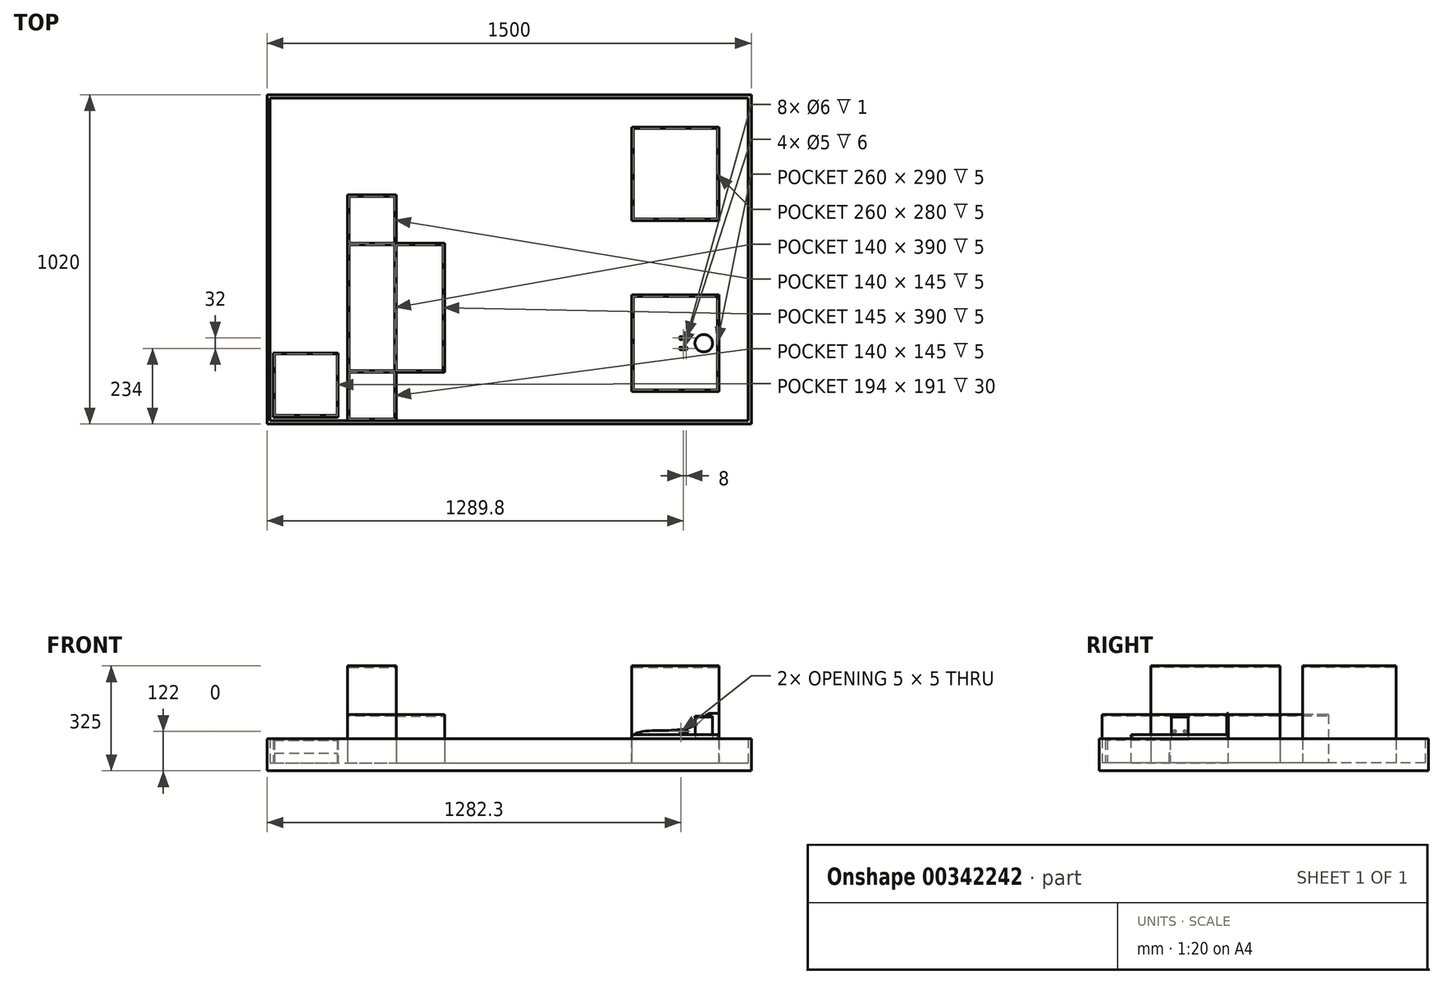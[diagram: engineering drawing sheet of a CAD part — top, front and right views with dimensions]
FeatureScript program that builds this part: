
annotation { "Feature Type Name" : "Feature", "Feature Type Description" : "" }
export const myFeature = defineFeature(function(context is Context, id is Id, definition is map)
    precondition{}
    {
        {
            var Q0;
            Q0=qCreatedBy(makeId("Top.planeOp"),FACE);
            var sketch = newSketch(context, id + "F0", { "sketchPlane" : qUnion([Q0])});
            skCircle(sketch, "E0", {"center": v(0, 0) * mm, "radius": 27.2 * mm});
            skSolve(sketch);
        }
        {
            var Q0;
            Q0=qSketchRegion(id+"F0",true);
            extrude(context, id + "F1", {"entities" : qUnion([Q0]), "depth" : 2.83 * mm});
        }
        {
            var Q0;
            Q0=makeQuery(id+"F1.opExtrude","CAP_FACE",FACE,{"disambiguationData":[OSD([sQuery(id+"F0.wireOp",EDGE,"E0")])],"isStart":false});
            var sketch = newSketch(context, id + "F2", { "sketchPlane" : qUnion([Q0])});
            skCircle(sketch, "E1", {"center": v(0, 0) * mm, "radius": 26.4 * mm});
            skSolve(sketch);
        }
        {
            var Q0;
            Q0=qSketchRegion(id+"F2",true);
            extrude(context, id + "F3", {"entities" : qUnion([Q0]), "operationType" : NewBodyOperationType.ADD, "depth" : 67.36 * mm});
        }
        {
            var Q0;
            Q0=makeQuery(id+"F3.opExtrude","CAP_FACE",FACE,{"disambiguationData":[OSD([sQuery(id+"F2.wireOp",EDGE,"E1")])],"isStart":false});
            var sketch = newSketch(context, id + "F4", { "sketchPlane" : qUnion([Q0])});
            skCircle(sketch, "E2", {"center": v(0, 0) * mm, "radius": 27.2 * mm});
            skSolve(sketch);
        }
        {
            var Q0;
            Q0=qSketchRegion(id+"F4",true);
            extrude(context, id + "F5", {"entities" : qUnion([Q0]), "operationType" : NewBodyOperationType.ADD, "depth" : 2.83 * mm});
        }
        {
            var Q0;
            Q0=makeQuery(id+"F5.opExtrude","CAP_FACE",FACE,{"disambiguationData":[OSD([sQuery(id+"F4.wireOp",EDGE,"E2")])],"isStart":false});
            var sketch = newSketch(context, id + "F6", { "sketchPlane" : qUnion([Q0])});
            skSolve(sketch);
        }
        {
            var Q0;
            Q0=qCreatedBy(makeId("Top.planeOp"),FACE);
            cPlane(context, id + "F7", {"entities" : qUnion([Q0]), "cplaneType" : CPlaneType.OFFSET, "offset" : 25 * mm, "width" : 150 * mm, "height" : 150 * mm});
        }
        {
            var Q0;
            Q0=makeQuery(id+"F6.imprint","IMPRINT",FACE,{"disambiguationData":[TD([[makeQuery(id+"F6.imprint","IMPRINT",EDGE,{"derivedFrom":makeQuery(id+"F5.opExtrude","CAP_EDGE",EDGE,{"disambiguationData":[OSD([sQuery(id+"F4.wireOp",EDGE,"E2")])],"isStart":false})}),1.0]])]});
            var sketch = newSketch(context, id + "F8", { "sketchPlane" : qUnion([Q0])});
            skSolve(sketch);
        }
        {
            var Q0;
            Q0=qCreatedBy(makeId("Top.planeOp"),FACE);
            var sketch = newSketch(context, id + "F9", { "sketchPlane" : qUnion([Q0])});
            skLineSegment(sketch, "E3.bottom", {"start": v(-222.8, -150) * mm, "end": v(47.2, -150) * mm});
            skLineSegment(sketch, "E3.top", {"start": v(-222.8, 150) * mm, "end": v(47.2, 150) * mm});
            skLineSegment(sketch, "E3.left", {"start": v(-222.8, -150) * mm, "end": v(-222.8, 150) * mm});
            skLineSegment(sketch, "E3.right", {"start": v(47.2, -150) * mm, "end": v(47.2, 150) * mm});
            skSolve(sketch);
        }
        {
            var Q0;
            Q0=qSketchRegion(id+"F9",true);
            extrude(context, id + "F10", {"entities" : qUnion([Q0]), "oppositeDirection" : true, "depth" : 72 * mm});
        }
        {
            var Q0;
            Q0=makeQuery(id+"F10.opExtrude","CAP_FACE",FACE,{"disambiguationData":[OSD([sQuery(id+"F9.wireOp",EDGE,"E3.bottom"),sQuery(id+"F9.wireOp",EDGE,"E3.top"),sQuery(id+"F9.wireOp",EDGE,"E3.left"),sQuery(id+"F9.wireOp",EDGE,"E3.right")])],"isStart":true});
            var sketch = newSketch(context, id + "F11", { "sketchPlane" : qUnion([Q0])});
            skLineSegment(sketch, "E4.bottom", {"start": v(-222.8, -150) * mm, "end": v(47.2, -150) * mm});
            skLineSegment(sketch, "E4.top", {"start": v(-222.8, -145) * mm, "end": v(42.2, -145) * mm});
            skLineSegment(sketch, "E4.left", {"start": v(-222.8, -150) * mm, "end": v(-222.8, -145) * mm});
            skLineSegment(sketch, "E5.bottom", {"start": v(47.2, 150) * mm, "end": v(42.2, 150) * mm});
            skLineSegment(sketch, "E5.left", {"start": v(47.2, 150) * mm, "end": v(47.2, -150) * mm});
            skLineSegment(sketch, "E5.right", {"start": v(42.2, 150) * mm, "end": v(42.2, -145) * mm});
            skSolve(sketch);
        }
        {
            var Q0;
            Q0=qSketchRegion(id+"F11",true);
            extrude(context, id + "F12", {"entities" : qUnion([Q0]), "operationType" : NewBodyOperationType.ADD, "depth" : 15 * mm});
        }
        {
            var Q0;
            Q0=makeQuery(id+"F12.boolean.opBoolean","MERGE",FACE,{"derivedFrom":[makeQuery(id+"F10.opExtrude","SWEPT_FACE",FACE,{"disambiguationData":[OSD([sQuery(id+"F9.wireOp",EDGE,"E3.top")])]}),makeQuery(id+"F12.opExtrude","SWEPT_FACE",FACE,{"disambiguationData":[OSD([sQuery(id+"F11.wireOp",EDGE,"E5.bottom")])]})]});
            var sketch = newSketch(context, id + "F13", { "sketchPlane" : qUnion([Q0])});
            skLineSegment(sketch, "E6", {"start": v(-47.2, 81.36) * mm, "end": v(-21.31, 81.36) * mm});
            skFitSpline(sketch, "E7", {"points": [v(-21.31, 81.36) * mm, v(15.24, 52.01) * mm, v(114.14, 28.17) * mm, v(222.8, 0) * mm], "startDerivative": vector(181.02, 0.3) * mm, "endDerivative": vector(-1.73, -239.85) * mm});
            skLineSegment(sketch, "E8", {"start": v(-47.2, 81.36) * mm, "end": v(-47.2, -72) * mm});
            skLineSegment(sketch, "E9", {"start": v(-47.2, -72) * mm, "end": v(222.8, -72) * mm});
            skLineSegment(sketch, "E10", {"start": v(222.8, -72) * mm, "end": v(222.8, 0) * mm});
            skSolve(sketch);
        }
        {
            var Q0;
            Q0=qSketchRegion(id+"F13",true);
            extrude(context, id + "F14", {"entities" : qUnion([Q0]), "operationType" : NewBodyOperationType.ADD, "oppositeDirection" : true, "depth" : 5 * mm});
        }
        {
            var Q0;
            Q0=makeQuery(id+"F10.opExtrude","CAP_FACE",FACE,{"disambiguationData":[OSD([sQuery(id+"F9.wireOp",EDGE,"E3.bottom"),sQuery(id+"F9.wireOp",EDGE,"E3.top"),sQuery(id+"F9.wireOp",EDGE,"E3.left"),sQuery(id+"F9.wireOp",EDGE,"E3.right")])],"isStart":true});
            var sketch = newSketch(context, id + "F15", { "sketchPlane" : qUnion([Q0])});
            skLineSegment(sketch, "E11.bottom", {"start": v(-222.8, 145) * mm, "end": v(-217.8, 145) * mm});
            skLineSegment(sketch, "E11.top", {"start": v(-222.8, -145) * mm, "end": v(-217.8, -145) * mm});
            skLineSegment(sketch, "E11.left", {"start": v(-222.8, 145) * mm, "end": v(-222.8, -145) * mm});
            skLineSegment(sketch, "E11.right", {"start": v(-217.8, 145) * mm, "end": v(-217.8, -145) * mm});
            skSolve(sketch);
        }
        {
            var Q0;
            Q0=qSketchRegion(id+"F15",true);
            extrude(context, id + "F16", {"entities" : qUnion([Q0]), "operationType" : NewBodyOperationType.ADD, "depth" : 5 * mm});
        }
        {
            var Q0;
            Q0=makeQuery(id+"F10.opExtrude","CAP_FACE",FACE,{"disambiguationData":[OSD([sQuery(id+"F9.wireOp",EDGE,"E3.bottom"),sQuery(id+"F9.wireOp",EDGE,"E3.top"),sQuery(id+"F9.wireOp",EDGE,"E3.left"),sQuery(id+"F9.wireOp",EDGE,"E3.right")])],"isStart":false});
            var sketch = newSketch(context, id + "F17", { "sketchPlane" : qUnion([Q0])});
            skLineSegment(sketch, "E12.bottom", {"start": v(147.2, 250) * mm, "end": v(-1352.8, 250) * mm});
            skLineSegment(sketch, "E12.top", {"start": v(147.2, -770) * mm, "end": v(-1352.8, -770) * mm});
            skLineSegment(sketch, "E12.left", {"start": v(147.2, 250) * mm, "end": v(147.2, -770) * mm});
            skLineSegment(sketch, "E12.right", {"start": v(-1352.8, 250) * mm, "end": v(-1352.8, -770) * mm});
            skSolve(sketch);
        }
        {
            var Q0;
            Q0=qSketchRegion(id+"F17",true);
            extrude(context, id + "F18", {"entities" : qUnion([Q0]), "operationType" : NewBodyOperationType.ADD, "depth" : 25 * mm});
        }
        {
            var Q0;
            Q0=makeQuery(id+"F18.opExtrude","CAP_FACE",FACE,{"disambiguationData":[OSD([sQuery(id+"F17.wireOp",EDGE,"E12.bottom"),sQuery(id+"F17.wireOp",EDGE,"E12.top"),sQuery(id+"F17.wireOp",EDGE,"E12.left"),sQuery(id+"F17.wireOp",EDGE,"E12.right")])],"isStart":true});
            var sketch = newSketch(context, id + "F19", { "sketchPlane" : qUnion([Q0])});
            skLineSegment(sketch, "E13.bottom", {"start": v(-222.8, 670) * mm, "end": v(47.2, 670) * mm});
            skLineSegment(sketch, "E13.top", {"start": v(-222.8, 380) * mm, "end": v(47.2, 380) * mm});
            skLineSegment(sketch, "E13.left", {"start": v(-222.8, 670) * mm, "end": v(-222.8, 380) * mm});
            skLineSegment(sketch, "E13.right", {"start": v(47.2, 670) * mm, "end": v(47.2, 380) * mm});
            skSolve(sketch);
        }
        {
            var Q0;
            Q0=qSketchRegion(id+"F19",true);
            extrude(context, id + "F20", {"entities" : qUnion([Q0]), "operationType" : NewBodyOperationType.ADD, "depth" : 300 * mm});
        }
        {
            var Q0;
            Q0=makeQuery(id+"F20.opExtrude","CAP_FACE",FACE,{"disambiguationData":[OSD([sQuery(id+"F19.wireOp",EDGE,"E13.bottom"),sQuery(id+"F19.wireOp",EDGE,"E13.top"),sQuery(id+"F19.wireOp",EDGE,"E13.left"),sQuery(id+"F19.wireOp",EDGE,"E13.right")])],"isStart":false});
            var sketch = newSketch(context, id + "F21", { "sketchPlane" : qUnion([Q0])});
            skLineSegment(sketch, "E14.bottom", {"start": v(-217.8, 665) * mm, "end": v(42.2, 665) * mm});
            skLineSegment(sketch, "E14.top", {"start": v(-217.8, 385) * mm, "end": v(42.2, 385) * mm});
            skLineSegment(sketch, "E14.left", {"start": v(-217.8, 665) * mm, "end": v(-217.8, 385) * mm});
            skLineSegment(sketch, "E14.right", {"start": v(42.2, 665) * mm, "end": v(42.2, 385) * mm});
            skSolve(sketch);
        }
        {
            var Q0;
            Q0=qSketchRegion(id+"F21",true);
            extrude(context, id + "F22", {"entities" : qUnion([Q0]), "operationType" : NewBodyOperationType.REMOVE, "oppositeDirection" : true, "depth" : 5 * mm});
        }
        {
            var Q0;
            Q0=makeQuery(id+"F18.opExtrude","CAP_FACE",FACE,{"disambiguationData":[OSD([sQuery(id+"F17.wireOp",EDGE,"E12.bottom"),sQuery(id+"F17.wireOp",EDGE,"E12.top"),sQuery(id+"F17.wireOp",EDGE,"E12.left"),sQuery(id+"F17.wireOp",EDGE,"E12.right")])],"isStart":true});
            var sketch = newSketch(context, id + "F23", { "sketchPlane" : qUnion([Q0])});
            skLineSegment(sketch, "E15.bottom", {"start": v(-1352.8, 770) * mm, "end": v(147.2, 770) * mm});
            skLineSegment(sketch, "E15.top", {"start": v(-1352.8, -250) * mm, "end": v(147.2, -250) * mm});
            skLineSegment(sketch, "E15.left", {"start": v(-1352.8, 770) * mm, "end": v(-1352.8, -250) * mm});
            skLineSegment(sketch, "E15.right", {"start": v(147.2, 770) * mm, "end": v(147.2, -250) * mm});
            skLineSegment(sketch, "E16.bottom", {"start": v(-1342.8, 760) * mm, "end": v(137.2, 760) * mm});
            skLineSegment(sketch, "E16.top", {"start": v(-1342.8, -240) * mm, "end": v(137.2, -240) * mm});
            skLineSegment(sketch, "E16.left", {"start": v(-1342.8, 760) * mm, "end": v(-1342.8, -240) * mm});
            skLineSegment(sketch, "E16.right", {"start": v(137.2, 760) * mm, "end": v(137.2, -240) * mm});
            skSolve(sketch);
        }
        {
            var Q0;
            Q0=qSketchRegion(id+"F23",true);
            extrude(context, id + "F24", {"entities" : qUnion([Q0]), "operationType" : NewBodyOperationType.ADD, "depth" : 75 * mm});
        }
        {
            var Q0;
            Q0=makeQuery(id+"F18.opExtrude","CAP_FACE",FACE,{"disambiguationData":[OSD([sQuery(id+"F17.wireOp",EDGE,"E12.bottom"),sQuery(id+"F17.wireOp",EDGE,"E12.top"),sQuery(id+"F17.wireOp",EDGE,"E12.left"),sQuery(id+"F17.wireOp",EDGE,"E12.right")])],"isStart":true});
            var sketch = newSketch(context, id + "F25", { "sketchPlane" : qUnion([Q0])});
            skLineSegment(sketch, "E17.bottom", {"start": v(-1102.8, 460) * mm, "end": v(-952.8, 460) * mm});
            skLineSegment(sketch, "E17.top", {"start": v(-1102.8, -240) * mm, "end": v(-952.8, -240) * mm});
            skLineSegment(sketch, "E17.left", {"start": v(-1102.8, 460) * mm, "end": v(-1102.8, -240) * mm});
            skLineSegment(sketch, "E17.right", {"start": v(-952.8, 460) * mm, "end": v(-952.8, 310) * mm});
            skLineSegment(sketch, "E18.bottom", {"start": v(-952.8, 310) * mm, "end": v(-802.8, 310) * mm});
            skLineSegment(sketch, "E18.top", {"start": v(-952.8, -90) * mm, "end": v(-802.8, -90) * mm});
            skLineSegment(sketch, "E18.right", {"start": v(-802.8, 310) * mm, "end": v(-802.8, -90) * mm});
            skLineSegment(sketch, "E19.trimOffspring", {"start": v(-952.8, -90) * mm, "end": v(-952.8, -240) * mm});
            skSolve(sketch);
        }
        {
            var Q0;
            Q0=qSketchRegion(id+"F25",true);
            extrude(context, id + "F26", {"entities" : qUnion([Q0]), "operationType" : NewBodyOperationType.ADD, "depth" : 150 * mm});
        }
        {
            var Q0;
            Q0=makeQuery(id+"F26.opExtrude","CAP_FACE",FACE,{"disambiguationData":[OSD([sQuery(id+"F25.wireOp",EDGE,"E17.bottom"),sQuery(id+"F25.wireOp",EDGE,"E17.top"),sQuery(id+"F25.wireOp",EDGE,"E17.left"),sQuery(id+"F25.wireOp",EDGE,"E17.right"),sQuery(id+"F25.wireOp",EDGE,"E18.bottom"),sQuery(id+"F25.wireOp",EDGE,"E18.top"),sQuery(id+"F25.wireOp",EDGE,"E18.right"),sQuery(id+"F25.wireOp",EDGE,"E19.trimOffspring")])],"isStart":false});
            var sketch = newSketch(context, id + "F27", { "sketchPlane" : qUnion([Q0])});
            skLineSegment(sketch, "E20.bottom", {"start": v(-952.8, 310) * mm, "end": v(-1102.8, 310) * mm});
            skLineSegment(sketch, "E20.top", {"start": v(-952.8, -90) * mm, "end": v(-1102.8, -90) * mm});
            skLineSegment(sketch, "E20.left", {"start": v(-952.8, 310) * mm, "end": v(-952.8, -90) * mm});
            skLineSegment(sketch, "E20.right", {"start": v(-1102.8, 310) * mm, "end": v(-1102.8, -90) * mm});
            skSolve(sketch);
        }
        {
            var Q0;
            Q0=qSketchRegion(id+"F27",true);
            extrude(context, id + "F28", {"entities" : qUnion([Q0]), "operationType" : NewBodyOperationType.ADD, "depth" : 150 * mm});
        }
        {
            var Q0;
            Q0=makeQuery(id+"F28.opExtrude","CAP_FACE",FACE,{"disambiguationData":[OSD([sQuery(id+"F27.wireOp",EDGE,"E20.bottom"),sQuery(id+"F27.wireOp",EDGE,"E20.top"),sQuery(id+"F27.wireOp",EDGE,"E20.left"),sQuery(id+"F27.wireOp",EDGE,"E20.right")])],"isStart":false});
            var sketch = newSketch(context, id + "F29", { "sketchPlane" : qUnion([Q0])});
            skLineSegment(sketch, "E21.bottom", {"start": v(-1097.8, 305) * mm, "end": v(-957.8, 305) * mm});
            skLineSegment(sketch, "E21.top", {"start": v(-1097.8, -85) * mm, "end": v(-957.8, -85) * mm});
            skLineSegment(sketch, "E21.left", {"start": v(-1097.8, 305) * mm, "end": v(-1097.8, -85) * mm});
            skLineSegment(sketch, "E21.right", {"start": v(-957.8, 305) * mm, "end": v(-957.8, -85) * mm});
            skSolve(sketch);
        }
        {
            var Q0;
            Q0=qSketchRegion(id+"F29",true);
            extrude(context, id + "F30", {"entities" : qUnion([Q0]), "operationType" : NewBodyOperationType.REMOVE, "oppositeDirection" : true, "depth" : 5 * mm});
        }
        {
            var Q0;
            {var subQ0=sQuery(id+"F25.wireOp",EDGE,"E17.left");var subQ1=sQuery(id+"F25.wireOp",EDGE,"E18.bottom");var subQ2=sQuery(id+"F25.wireOp",EDGE,"E17.right");var subQ3=sQuery(id+"F25.wireOp",EDGE,"E17.bottom");var subQ4=makeQuery(id+"F26.opExtrude","CAP_FACE",FACE,{"disambiguationData":[OSD([subQ3,sQuery(id+"F25.wireOp",EDGE,"E17.top"),subQ0,subQ2,subQ1,sQuery(id+"F25.wireOp",EDGE,"E18.top"),sQuery(id+"F25.wireOp",EDGE,"E18.right"),sQuery(id+"F25.wireOp",EDGE,"E19.trimOffspring")])],"isStart":false});Q0=makeQuery(id+"F28.boolean.opBoolean","SPLIT",FACE,{"disambiguationData":[TD([makeQuery(id+"F26.opExtrude","SWEPT_FACE",FACE,{"disambiguationData":[OSD([subQ3])]})])],"derivedFrom":subQ4});}
            var sketch = newSketch(context, id + "F31", { "sketchPlane" : qUnion([Q0])});
            skLineSegment(sketch, "E22.bottom", {"start": v(-1097.8, 455) * mm, "end": v(-957.8, 455) * mm});
            skLineSegment(sketch, "E22.top", {"start": v(-1097.8, 310) * mm, "end": v(-957.8, 310) * mm});
            skLineSegment(sketch, "E22.left", {"start": v(-1097.8, 455) * mm, "end": v(-1097.8, 310) * mm});
            skLineSegment(sketch, "E22.right", {"start": v(-957.8, 455) * mm, "end": v(-957.8, 310) * mm});
            skLineSegment(sketch, "E23.bottom", {"start": v(-952.8, 305) * mm, "end": v(-807.8, 305) * mm});
            skLineSegment(sketch, "E23.top", {"start": v(-952.8, -85) * mm, "end": v(-807.8, -85) * mm});
            skLineSegment(sketch, "E23.left", {"start": v(-952.8, 305) * mm, "end": v(-952.8, -85) * mm});
            skLineSegment(sketch, "E23.right", {"start": v(-807.8, 305) * mm, "end": v(-807.8, -85) * mm});
            skLineSegment(sketch, "E24.bottom", {"start": v(-1097.8, -90) * mm, "end": v(-957.8, -90) * mm});
            skLineSegment(sketch, "E24.top", {"start": v(-1097.8, -235) * mm, "end": v(-957.8, -235) * mm});
            skLineSegment(sketch, "E24.left", {"start": v(-1097.8, -90) * mm, "end": v(-1097.8, -235) * mm});
            skLineSegment(sketch, "E24.right", {"start": v(-957.8, -90) * mm, "end": v(-957.8, -235) * mm});
            skSolve(sketch);
        }
        {
            var Q0;
            Q0=qSketchRegion(id+"F31",true);
            extrude(context, id + "F32", {"entities" : qUnion([Q0]), "operationType" : NewBodyOperationType.REMOVE, "oppositeDirection" : true, "depth" : 5 * mm});
        }
        {
            var Q0;
            Q0=qCreatedBy(id+"F7.planeOp",FACE);
            var sketch = newSketch(context, id + "F33", { "sketchPlane" : qUnion([Q0])});
            skLineSegment(sketch, "E25", {"start": v(0, 0) * mm, "end": v(-90, 0) * mm, "construction": true});
            skLineSegment(sketch, "E26.bottom", {"start": v(-74.5, -12) * mm, "end": v(-55, -12) * mm});
            skLineSegment(sketch, "E26.top", {"start": v(-74.5, -20) * mm, "end": v(-55, -20) * mm});
            skLineSegment(sketch, "E26.left", {"start": v(-74.5, -12) * mm, "end": v(-74.5, -13) * mm});
            skPoint(sketch, "E27.visualSharp", {"position": v(-51, -12) * mm});
            skPoint(sketch, "E28.visualSharp", {"position": v(-51, -20) * mm});
            skCircle(sketch, "E29", {"center": v(-55, -16) * mm, "radius": 3 * mm});
            skLineSegment(sketch, "E30", {"start": v(-59, -3.98) * mm, "end": v(-59, -18.08) * mm, "construction": true});
            skCircle(sketch, "E31.MirrorC", {"center": v(-63, -16) * mm, "radius": 3 * mm});
            skLineSegment(sketch, "E32.bottom", {"start": v(-74.5, -13) * mm, "end": v(-65.65, -13) * mm});
            skLineSegment(sketch, "E32.top", {"start": v(-74.5, -19) * mm, "end": v(-65.65, -19) * mm});
            skArc(sketch, "E33", {"start": v(-65.65, -13) * mm, "mid": v(-67, -16) * mm, "end": v(-65.65, -19) * mm});
            skLineSegment(sketch, "E34.trimOffspring", {"start": v(-74.5, -19) * mm, "end": v(-74.5, -20) * mm});
            skArc(sketch, "E35.trimOffspring", {"start": v(-55, -20) * mm, "mid": v(-51, -16) * mm, "end": v(-55, -12) * mm});
            skLineSegment(sketch, "E36.MirrorCS", {"start": v(-74.5, 12) * mm, "end": v(-74.5, 13) * mm});
            skLineSegment(sketch, "E37.MirrorCS", {"start": v(-74.5, 19) * mm, "end": v(-74.5, 20) * mm});
            skPoint(sketch, "E38.MirrorP", {"position": v(-51, 12) * mm});
            skLineSegment(sketch, "E39.MirrorCS", {"start": v(-74.5, 12) * mm, "end": v(-55, 12) * mm});
            skPoint(sketch, "E40.MirrorP", {"position": v(-51, 20) * mm});
            skArc(sketch, "E41.MirrorCS", {"start": v(-65.65, 13) * mm, "mid": v(-67, 16) * mm, "end": v(-65.65, 19) * mm});
            skArc(sketch, "E42.MirrorCS", {"start": v(-55, 20) * mm, "mid": v(-51, 16) * mm, "end": v(-55, 12) * mm});
            skLineSegment(sketch, "E43.MirrorCS", {"start": v(-74.5, 20) * mm, "end": v(-55, 20) * mm});
            skCircle(sketch, "E44.MirrorC", {"center": v(-55, 16) * mm, "radius": 3 * mm});
            skCircle(sketch, "E45.MirrorC", {"center": v(-63, 16) * mm, "radius": 3 * mm});
            skLineSegment(sketch, "E46.MirrorCS", {"start": v(-74.5, 19) * mm, "end": v(-65.65, 19) * mm});
            skLineSegment(sketch, "E47.MirrorCS", {"start": v(-74.5, 13) * mm, "end": v(-65.65, 13) * mm});
            skSolve(sketch);
        }
        {
            var Q0;
            Q0=qSketchRegion(id+"F33",true);
            var Q1;
            Q1=qSketchRegion(id+"F36",true);
            extrude(context, id + "F34", {"entities" : qUnion([Q0, Q1]), "depth" : 8 * mm, "symmetric" : true});
        }
        {
            var Q0;
            Q0=makeQuery(id+"F34.opExtrude","CAP_EDGE",EDGE,{"disambiguationData":[OSD([sQuery(id+"F33.wireOp",EDGE,"E34.trimOffspring")])],"isStart":false});
            var Q1;
            Q1=makeQuery(id+"F34.opExtrude","CAP_EDGE",EDGE,{"disambiguationData":[OSD([sQuery(id+"F33.wireOp",EDGE,"E26.left")])],"isStart":false});
            var Q2;
            Q2=makeQuery(id+"F34.opExtrude","CAP_EDGE",EDGE,{"disambiguationData":[OSD([sQuery(id+"F33.wireOp",EDGE,"E34.trimOffspring")])],"isStart":true});
            var Q3;
            Q3=makeQuery(id+"F34.opExtrude","CAP_EDGE",EDGE,{"disambiguationData":[OSD([sQuery(id+"F33.wireOp",EDGE,"E26.left")])],"isStart":true});
            var Q4;
            Q4=makeQuery(id+"F34.opExtrude","CAP_EDGE",EDGE,{"disambiguationData":[OSD([sQuery(id+"F33.wireOp",EDGE,"E36.MirrorCS")])],"isStart":false});
            var Q5;
            Q5=makeQuery(id+"F34.opExtrude","CAP_EDGE",EDGE,{"disambiguationData":[OSD([sQuery(id+"F33.wireOp",EDGE,"E37.MirrorCS")])],"isStart":false});
            var Q6;
            Q6=makeQuery(id+"F34.opExtrude","CAP_EDGE",EDGE,{"disambiguationData":[OSD([sQuery(id+"F33.wireOp",EDGE,"E37.MirrorCS")])],"isStart":true});
            var Q7;
            Q7=makeQuery(id+"F34.opExtrude","CAP_EDGE",EDGE,{"disambiguationData":[OSD([sQuery(id+"F33.wireOp",EDGE,"E36.MirrorCS")])],"isStart":true});
            fillet(context, id + "F35", {"entities" : qUnion([Q0, Q1, Q2, Q3, Q4, Q5, Q6, Q7]), "radius" : 4 * mm, "tangentPropagation" : true, "allowEdgeOverflow" : false});
        }
        {
            var Q0;
            Q0=makeQuery(id+"F34.opExtrude","SWEPT_FACE",FACE,{"disambiguationData":[OSD([sQuery(id+"F33.wireOp",EDGE,"E26.top")])]});
            var sketch = newSketch(context, id + "F36", { "sketchPlane" : qUnion([Q0])});
            skCircle(sketch, "E48", {"center": v(-70.5, 25) * mm, "radius": 3 * mm});
            skSolve(sketch);
        }
        {
            var Q0;
            Q0=qSketchRegion(id+"F36",true);
            var Q1;
            Q1=makeQuery(id+"F34.opExtrude","SWEPT_FACE",FACE,{"disambiguationData":[OSD([sQuery(id+"F33.wireOp",EDGE,"E26.bottom")])]});
            extrude(context, id + "F37", {"entities" : qUnion([Q0]), "operationType" : NewBodyOperationType.ADD, "endBound" : BoundingType.UP_TO_SURFACE, "oppositeDirection" : true, "endBoundEntityFace" : qUnion([Q1]), "depth" : 25 * mm});
        }
        {
            var Q0;
            Q0=makeQuery(id+"F34.opExtrude","SWEPT_FACE",FACE,{"disambiguationData":[OSD([sQuery(id+"F33.wireOp",EDGE,"E43.MirrorCS")])]});
            var sketch = newSketch(context, id + "F38", { "sketchPlane" : qUnion([Q0])});
            skCircle(sketch, "E49", {"center": v(70.5, 25) * mm, "radius": 3 * mm});
            skSolve(sketch);
        }
        {
            var Q0;
            Q0=qSketchRegion(id+"F38",true);
            var Q1;
            Q1=makeQuery(id+"F34.opExtrude","SWEPT_FACE",FACE,{"disambiguationData":[OSD([sQuery(id+"F33.wireOp",EDGE,"E39.MirrorCS")])]});
            extrude(context, id + "F39", {"entities" : qUnion([Q0]), "operationType" : NewBodyOperationType.ADD, "endBound" : BoundingType.UP_TO_SURFACE, "oppositeDirection" : true, "endBoundEntityFace" : qUnion([Q1]), "depth" : 25 * mm});
        }
        {
            var Q0;
            Q0=qCreatedBy(id+"F7.planeOp",FACE);
            var sketch = newSketch(context, id + "F40", { "sketchPlane" : qUnion([Q0])});
            skCircle(sketch, "E50", {"center": v(-55, 16) * mm, "radius": 3 * mm});
            skCircle(sketch, "E51", {"center": v(-63, 16) * mm, "radius": 2.5 * mm});
            skCircle(sketch, "E52", {"center": v(-63, 16) * mm, "radius": 3 * mm});
            skCircle(sketch, "E53", {"center": v(-55, 16) * mm, "radius": 2.5 * mm});
            skSolve(sketch);
        }
        {
            var Q0;
            Q0=qSketchRegion(id+"F40",true);
            extrude(context, id + "F41", {"entities" : qUnion([Q0]), "operationType" : NewBodyOperationType.ADD, "depth" : 6 * mm, "symmetric" : true});
        }
        {
            var Q0;
            Q0=qCreatedBy(id+"F7.planeOp",FACE);
            var sketch = newSketch(context, id + "F42", { "sketchPlane" : qUnion([Q0])});
            skCircle(sketch, "E54", {"center": v(-63, -16) * mm, "radius": 2.5 * mm});
            skCircle(sketch, "E55", {"center": v(-63, -16) * mm, "radius": 3 * mm});
            skCircle(sketch, "E56", {"center": v(-55, -16) * mm, "radius": 2.5 * mm});
            skCircle(sketch, "E57", {"center": v(-55, -16) * mm, "radius": 3 * mm});
            skSolve(sketch);
        }
        {
            var Q0;
            Q0=qSketchRegion(id+"F42",true);
            extrude(context, id + "F43", {"entities" : qUnion([Q0]), "operationType" : NewBodyOperationType.ADD, "depth" : 6 * mm, "symmetric" : true});
        }
        {
            var Q0;
            Q0=makeQuery(id+"F34.opExtrude","SWEPT_FACE",FACE,{"disambiguationData":[OSD([sQuery(id+"F33.wireOp",EDGE,"E43.MirrorCS")])]});
            var sketch = newSketch(context, id + "F44", { "sketchPlane" : qUnion([Q0])});
            skArc(sketch, "E58", {"start": v(71.5, 27.3) * mm, "mid": v(70.5, 27.5) * mm, "end": v(69.5, 27.3) * mm});
            skLineSegment(sketch, "E59.bottom", {"start": v(68.2, 26) * mm, "end": v(69.5, 26) * mm});
            skLineSegment(sketch, "E59.top", {"start": v(68.2, 24) * mm, "end": v(69.5, 24) * mm});
            skLineSegment(sketch, "E60.left", {"start": v(71.5, 27.3) * mm, "end": v(71.5, 26) * mm});
            skLineSegment(sketch, "E60.right", {"start": v(69.5, 27.3) * mm, "end": v(69.5, 26) * mm});
            skPoint(sketch, "E61.orphan", {"position": v(69.5, 27.8) * mm});
            skPoint(sketch, "E62.orphan", {"position": v(71.5, 27.8) * mm});
            skArc(sketch, "E63.trimOffspring", {"start": v(68.2, 26) * mm, "mid": v(68, 25) * mm, "end": v(68.2, 24) * mm});
            skPoint(sketch, "E59.left.start.orphan", {"position": v(67.32, 26) * mm});
            skPoint(sketch, "E64.orphan", {"position": v(67.32, 24) * mm});
            skArc(sketch, "E65.trimOffspring", {"start": v(69.5, 22.7) * mm, "mid": v(70.5, 22.5) * mm, "end": v(71.5, 22.7) * mm});
            skLineSegment(sketch, "E66.trimOffspring", {"start": v(69.5, 24) * mm, "end": v(69.5, 22.7) * mm});
            skLineSegment(sketch, "E67.trimOffspring", {"start": v(71.5, 26) * mm, "end": v(72.8, 26) * mm});
            skLineSegment(sketch, "E68.trimOffspring", {"start": v(71.5, 24) * mm, "end": v(71.5, 22.7) * mm});
            skLineSegment(sketch, "E69.trimOffspring", {"start": v(71.5, 24) * mm, "end": v(72.8, 24) * mm});
            skPoint(sketch, "E60.top.end.orphan", {"position": v(69.5, 22.2) * mm});
            skPoint(sketch, "E70.orphan", {"position": v(71.5, 22.2) * mm});
            skPoint(sketch, "E59.right.end.orphan", {"position": v(73.68, 24) * mm});
            skPoint(sketch, "E71.orphan", {"position": v(73.68, 26) * mm});
            skArc(sketch, "E72.trimOffspring", {"start": v(72.8, 24) * mm, "mid": v(73, 25) * mm, "end": v(72.8, 26) * mm});
            skSolve(sketch);
        }
        {
            var Q0;
            Q0=qSketchRegion(id+"F44",true);
            extrude(context, id + "F45", {"entities" : qUnion([Q0]), "operationType" : NewBodyOperationType.REMOVE, "endBound" : BoundingType.THROUGH_ALL, "oppositeDirection" : true, "depth" : 25 * mm});
        }
        {
            var Q0;
            Q0=makeQuery(id+"F18.opExtrude","CAP_FACE",FACE,{"disambiguationData":[OSD([sQuery(id+"F17.wireOp",EDGE,"E12.bottom"),sQuery(id+"F17.wireOp",EDGE,"E12.top"),sQuery(id+"F17.wireOp",EDGE,"E12.left"),sQuery(id+"F17.wireOp",EDGE,"E12.right")])],"isStart":true});
            var sketch = newSketch(context, id + "F46", { "sketchPlane" : qUnion([Q0])});
            skLineSegment(sketch, "E73.bottom", {"start": v(-1332.8, -30) * mm, "end": v(-1132.8, -30) * mm});
            skLineSegment(sketch, "E73.top", {"start": v(-1332.8, -230) * mm, "end": v(-1132.8, -230) * mm});
            skLineSegment(sketch, "E73.left", {"start": v(-1332.8, -30) * mm, "end": v(-1332.8, -230) * mm});
            skLineSegment(sketch, "E73.right", {"start": v(-1132.8, -30) * mm, "end": v(-1132.8, -230) * mm});
            skLineSegment(sketch, "E74.bottom", {"start": v(-1329.8, -33) * mm, "end": v(-1135.8, -33) * mm});
            skLineSegment(sketch, "E74.top", {"start": v(-1329.8, -224) * mm, "end": v(-1135.8, -224) * mm});
            skLineSegment(sketch, "E74.left", {"start": v(-1329.8, -33) * mm, "end": v(-1329.8, -224) * mm});
            skLineSegment(sketch, "E74.right", {"start": v(-1135.8, -33) * mm, "end": v(-1135.8, -224) * mm});
            skSolve(sketch);
        }
        {
            var Q0;
            Q0=qSketchRegion(id+"F46",true);
            extrude(context, id + "F47", {"entities" : qUnion([Q0]), "operationType" : NewBodyOperationType.ADD, "depth" : 30 * mm});
        }
        {
            var Q0;
            Q0=makeQuery(id+"F47.opExtrude","CAP_FACE",FACE,{"disambiguationData":[OSD([sQuery(id+"F46.wireOp",EDGE,"E73.bottom"),sQuery(id+"F46.wireOp",EDGE,"E73.top"),sQuery(id+"F46.wireOp",EDGE,"E73.left"),sQuery(id+"F46.wireOp",EDGE,"E73.right"),sQuery(id+"F46.wireOp",EDGE,"E74.bottom"),sQuery(id+"F46.wireOp",EDGE,"E74.top"),sQuery(id+"F46.wireOp",EDGE,"E74.left"),sQuery(id+"F46.wireOp",EDGE,"E74.right")])],"isStart":false});
            var sketch = newSketch(context, id + "F48", { "sketchPlane" : qUnion([Q0])});
            skLineSegment(sketch, "E75.bottom", {"start": v(-1332.8, -30) * mm, "end": v(-1329.8, -30) * mm});
            skLineSegment(sketch, "E75.top", {"start": v(-1332.8, -230) * mm, "end": v(-1329.8, -230) * mm});
            skLineSegment(sketch, "E75.left", {"start": v(-1332.8, -30) * mm, "end": v(-1332.8, -230) * mm});
            skLineSegment(sketch, "E75.right", {"start": v(-1329.8, -30) * mm, "end": v(-1329.8, -224) * mm});
            skLineSegment(sketch, "E76.bottom", {"start": v(-1329.8, -230) * mm, "end": v(-1135.8, -230) * mm});
            skLineSegment(sketch, "E76.top", {"start": v(-1329.8, -224) * mm, "end": v(-1135.8, -224) * mm});
            skLineSegment(sketch, "E77.bottom", {"start": v(-1135.8, -230) * mm, "end": v(-1132.8, -230) * mm});
            skLineSegment(sketch, "E77.top", {"start": v(-1135.8, -30) * mm, "end": v(-1132.8, -30) * mm});
            skLineSegment(sketch, "E77.left", {"start": v(-1135.8, -224) * mm, "end": v(-1135.8, -30) * mm});
            skLineSegment(sketch, "E77.right", {"start": v(-1132.8, -230) * mm, "end": v(-1132.8, -30) * mm});
            skSolve(sketch);
        }
        {
            var Q0;
            Q0=qSketchRegion(id+"F48",true);
            extrude(context, id + "F49", {"entities" : qUnion([Q0]), "operationType" : NewBodyOperationType.ADD, "depth" : 40 * mm});
        }
        {
            var Q0;
            Q0=makeQuery(id+"F34.opExtrude","CAP_FACE",FACE,{"disambiguationData":[OSD([sQuery(id+"F33.wireOp",EDGE,"E36.MirrorCS"),sQuery(id+"F33.wireOp",EDGE,"E37.MirrorCS"),sQuery(id+"F33.wireOp",EDGE,"E39.MirrorCS"),sQuery(id+"F33.wireOp",EDGE,"E41.MirrorCS"),sQuery(id+"F33.wireOp",EDGE,"E42.MirrorCS"),sQuery(id+"F33.wireOp",EDGE,"E43.MirrorCS"),sQuery(id+"F33.wireOp",EDGE,"E44.MirrorC"),sQuery(id+"F33.wireOp",EDGE,"E45.MirrorC"),sQuery(id+"F33.wireOp",EDGE,"E46.MirrorCS"),sQuery(id+"F33.wireOp",EDGE,"E47.MirrorCS")])],"isStart":false});
            var sketch = newSketch(context, id + "F50", { "sketchPlane" : qUnion([Q0])});
            skLineSegment(sketch, "E78.bottom", {"start": v(-78.97, 27.08) * mm, "end": v(-0.62, 27.08) * mm});
            skLineSegment(sketch, "E78.top", {"start": v(-78.97, -29.9) * mm, "end": v(-0.62, -29.9) * mm});
            skLineSegment(sketch, "E78.left", {"start": v(-78.97, 27.08) * mm, "end": v(-78.97, 12) * mm});
            skLineSegment(sketch, "E78.right", {"start": v(-0.62, 27.08) * mm, "end": v(-0.62, -29.9) * mm});
            skLineSegment(sketch, "E79.bottom", {"start": v(-78.97, 12) * mm, "end": v(-44.82, 12) * mm});
            skLineSegment(sketch, "E79.top", {"start": v(-78.97, -8.24) * mm, "end": v(-44.82, -8.24) * mm});
            skLineSegment(sketch, "E79.right", {"start": v(-44.82, 12) * mm, "end": v(-44.82, -8.24) * mm});
            skLineSegment(sketch, "E80.trimOffspring", {"start": v(-78.97, -8.24) * mm, "end": v(-78.97, -29.9) * mm});
            skCircle(sketch, "E81", {"center": v(-63, 16) * mm, "radius": 2.5 * mm});
            skSolve(sketch);
        }
        {
            var Q0;
            Q0=qSketchRegion(id+"F50",true);
            extrude(context, id + "F51", {"entities" : qUnion([Q0]), "depth" : 8 * mm});
        }
        {
            var Q0;
            Q0=makeQuery(id+"F51.opExtrude","SWEPT_BODY",BODY,{"disambiguationData":[OSD([sQuery(id+"F50.wireOp",EDGE,"E78.bottom"),sQuery(id+"F50.wireOp",EDGE,"E78.top"),sQuery(id+"F50.wireOp",EDGE,"E78.left"),sQuery(id+"F50.wireOp",EDGE,"E78.right"),sQuery(id+"F50.wireOp",EDGE,"E79.bottom"),sQuery(id+"F50.wireOp",EDGE,"E79.top"),sQuery(id+"F50.wireOp",EDGE,"E79.right"),sQuery(id+"F50.wireOp",EDGE,"E80.trimOffspring"),sQuery(id+"F50.wireOp",EDGE,"E81")])]});
            deleteBodies(context, id + "F52", {"entities" : qUnion([Q0])});
        }
    });
